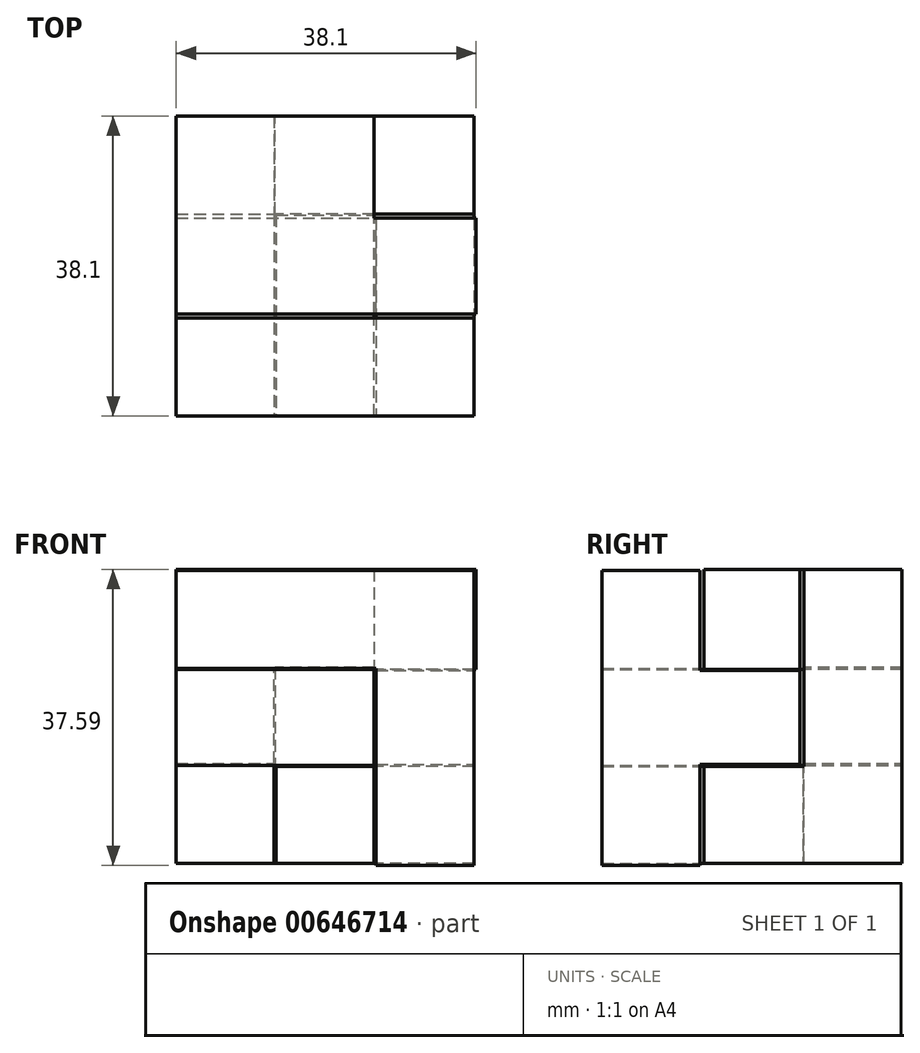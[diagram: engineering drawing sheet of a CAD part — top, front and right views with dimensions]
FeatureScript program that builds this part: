
annotation { "Feature Type Name" : "Feature", "Feature Type Description" : "" }
export const myFeature = defineFeature(function(context is Context, id is Id, definition is map)
    precondition{}
    {
        {
            var Q0;
            Q0=qCreatedBy(makeId("Top.planeOp"),FACE);
            var sketch = newSketch(context, id + "F0", { "sketchPlane" : qUnion([Q0])});
            skLineSegment(sketch, "E0.bottom", {"start": v(0, 0) * mm, "end": v(25.15, 0) * mm});
            skLineSegment(sketch, "E0.top", {"start": v(0, 25.15) * mm, "end": v(25.15, 25.15) * mm});
            skLineSegment(sketch, "E0.left", {"start": v(0, 0) * mm, "end": v(0, 25.15) * mm});
            skLineSegment(sketch, "E0.right", {"start": v(25.15, 0) * mm, "end": v(25.15, 25.15) * mm});
            skSolve(sketch);
        }
        {
            var Q0;
            Q0 = qSketchRegion(id + "F0", true);
            extrude(context, id + "F1", {"entities" : qUnion([Q0]), "depth" : 12.2 * mm, "offsetDistance" : 25.4 * mm});
        }
        {
            var Q0;
            Q0=qCreatedBy(makeId("Top.planeOp"),FACE);
            var sketch = newSketch(context, id + "F2", { "sketchPlane" : qUnion([Q0])});
            skLineSegment(sketch, "E1", {"start": v(0, 0) * mm, "end": v(0, 38.1) * mm});
            skLineSegment(sketch, "E2", {"start": v(0, 38.1) * mm, "end": v(25.15, 38.1) * mm});
            skLineSegment(sketch, "E3", {"start": v(25.15, 38.1) * mm, "end": v(25.15, 25.65) * mm});
            skLineSegment(sketch, "E4", {"start": v(25.15, 25.65) * mm, "end": v(12.45, 25.65) * mm});
            skLineSegment(sketch, "E5", {"start": v(12.45, 25.65) * mm, "end": v(12.45, 0) * mm});
            skLineSegment(sketch, "E6", {"start": v(12.45, 0) * mm, "end": v(0, 0) * mm});
            skSolve(sketch);
        }
        {
            var Q0;
            Q0 = qSketchRegion(id + "F2", true);
            extrude(context, id + "F3", {"entities" : qUnion([Q0]), "oppositeDirection" : true, "depth" : 12.45 * mm, "offsetDistance" : 25.4 * mm});
        }
        {
            var Q0;
            Q0=makeQuery(id+"F3.opExtrude","CAP_FACE",FACE,{"disambiguationData":[OSD([sQuery(id+"F2.wireOp",EDGE,"E1"),sQuery(id+"F2.wireOp",EDGE,"E2"),sQuery(id+"F2.wireOp",EDGE,"E3"),sQuery(id+"F2.wireOp",EDGE,"E4"),sQuery(id+"F2.wireOp",EDGE,"E5"),sQuery(id+"F2.wireOp",EDGE,"E6")])],"isStart":true});
            var sketch = newSketch(context, id + "F4", { "sketchPlane" : qUnion([Q0])});
            skLineSegment(sketch, "E7.bottom", {"start": v(25.15, 25.65) * mm, "end": v(12.57, 25.65) * mm});
            skLineSegment(sketch, "E7.top", {"start": v(25.15, 38.1) * mm, "end": v(12.57, 38.1) * mm});
            skLineSegment(sketch, "E7.left", {"start": v(25.15, 25.65) * mm, "end": v(25.15, 38.1) * mm});
            skLineSegment(sketch, "E7.right", {"start": v(12.57, 25.65) * mm, "end": v(12.57, 38.1) * mm});
            skSolve(sketch);
        }
        {
            var Q0;
            Q0 = qSketchRegion(id + "F4", true);
            extrude(context, id + "F5", {"entities" : qUnion([Q0]), "operationType" : NewBodyOperationType.ADD, "depth" : 12.45 * mm, "offsetDistance" : 25.4 * mm});
        }
        {
            var Q0;
            Q0=makeQuery(id+"F1.opExtrude","CAP_FACE",FACE,{"disambiguationData":[OSD([sQuery(id+"F0.wireOp",EDGE,"E0.bottom"),sQuery(id+"F0.wireOp",EDGE,"E0.top"),sQuery(id+"F0.wireOp",EDGE,"E0.left"),sQuery(id+"F0.wireOp",EDGE,"E0.right")])],"isStart":false});
            var sketch = newSketch(context, id + "F6", { "sketchPlane" : qUnion([Q0])});
            skLineSegment(sketch, "E8", {"start": v(0, 38.1) * mm, "end": v(25.15, 38.1) * mm});
            skLineSegment(sketch, "E9", {"start": v(25.15, 38.1) * mm, "end": v(25.15, 25.15) * mm});
            skLineSegment(sketch, "E10", {"start": v(25.15, 25.15) * mm, "end": v(38.1, 25.15) * mm});
            skLineSegment(sketch, "E11", {"start": v(38.1, 25.15) * mm, "end": v(38.1, 12.95) * mm});
            skLineSegment(sketch, "E12", {"start": v(38.1, 12.95) * mm, "end": v(12.95, 12.95) * mm});
            skLineSegment(sketch, "E13", {"start": v(12.95, 12.95) * mm, "end": v(12.95, 25.15) * mm, "construction": true});
            skLineSegment(sketch, "E14", {"start": v(12.95, 25.15) * mm, "end": v(0, 25.15) * mm, "construction": true});
            skLineSegment(sketch, "E15", {"start": v(0, 25.15) * mm, "end": v(0, 38.1) * mm});
            skLineSegment(sketch, "E16", {"start": v(12.95, 12.95) * mm, "end": v(0, 12.95) * mm});
            skLineSegment(sketch, "E17", {"start": v(0, 12.95) * mm, "end": v(0, 25.15) * mm});
            skSolve(sketch);
        }
        {
            var Q0;
            Q0 = qSketchRegion(id + "F6", true);
            extrude(context, id + "F7", {"entities" : qUnion([Q0]), "depth" : 12.7 * mm, "offsetDistance" : 25.4 * mm});
        }
        {
            var Q0;
            Q0=makeQuery(id+"F7.opExtrude","CAP_FACE",FACE,{"disambiguationData":[OSD([sQuery(id+"F6.wireOp",EDGE,"E8"),sQuery(id+"F6.wireOp",EDGE,"E9"),sQuery(id+"F6.wireOp",EDGE,"E10"),sQuery(id+"F6.wireOp",EDGE,"E11"),sQuery(id+"F6.wireOp",EDGE,"E12"),sQuery(id+"F6.wireOp",EDGE,"E13"),sQuery(id+"F6.wireOp",EDGE,"E14"),sQuery(id+"F6.wireOp",EDGE,"E15")])],"isStart":true});
            var sketch = newSketch(context, id + "F8", { "sketchPlane" : qUnion([Q0])});
            skLineSegment(sketch, "E18.bottom", {"start": v(0, -38.1) * mm, "end": v(12.45, -38.1) * mm});
            skLineSegment(sketch, "E18.top", {"start": v(0, -25.65) * mm, "end": v(12.45, -25.65) * mm});
            skLineSegment(sketch, "E18.left", {"start": v(0, -38.1) * mm, "end": v(0, -25.65) * mm});
            skLineSegment(sketch, "E18.right", {"start": v(12.45, -38.1) * mm, "end": v(12.45, -25.65) * mm});
            skSolve(sketch);
        }
        {
            var Q0;
            Q0 = qSketchRegion(id + "F8", true);
            extrude(context, id + "F9", {"entities" : qUnion([Q0]), "operationType" : NewBodyOperationType.ADD, "depth" : 11.94 * mm, "offsetDistance" : 25.4 * mm});
        }
        {
            var Q0;
            Q0=makeQuery(id+"F5.boolean.opBoolean","MERGE",FACE,{"derivedFrom":[makeQuery(id+"F3.opExtrude","SWEPT_FACE",FACE,{"disambiguationData":[OSD([sQuery(id+"F2.wireOp",EDGE,"E3")])]}),makeQuery(id+"F5.opExtrude","SWEPT_FACE",FACE,{"disambiguationData":[OSD([sQuery(id+"F4.wireOp",EDGE,"E7.left")])]})]});
            var sketch = newSketch(context, id + "F10", { "sketchPlane" : qUnion([Q0])});
            skLineSegment(sketch, "E19", {"start": v(38.1, -12.45) * mm, "end": v(38.1, 24.9) * mm});
            skLineSegment(sketch, "E20", {"start": v(38.1, 24.9) * mm, "end": v(25.65, 24.9) * mm});
            skLineSegment(sketch, "E21", {"start": v(25.65, 24.9) * mm, "end": v(25.65, -0.13) * mm});
            skLineSegment(sketch, "E22", {"start": v(25.65, -0.13) * mm, "end": v(12.95, -0.13) * mm});
            skLineSegment(sketch, "E23", {"start": v(12.95, -0.13) * mm, "end": v(12.95, -12.45) * mm});
            skLineSegment(sketch, "E24", {"start": v(12.95, -12.45) * mm, "end": v(38.1, -12.45) * mm});
            skSolve(sketch);
        }
        {
            var Q0;
            Q0 = qSketchRegion(id + "F10", true);
            extrude(context, id + "F11", {"entities" : qUnion([Q0]), "depth" : 12.7 * mm, "offsetDistance" : 25.4 * mm});
        }
        {
            var Q0;
            Q0=makeQuery(id+"F11.opExtrude","CAP_FACE",FACE,{"disambiguationData":[OSD([sQuery(id+"F10.wireOp",EDGE,"E19"),sQuery(id+"F10.wireOp",EDGE,"E20"),sQuery(id+"F10.wireOp",EDGE,"E21"),sQuery(id+"F10.wireOp",EDGE,"E22"),sQuery(id+"F10.wireOp",EDGE,"E23"),sQuery(id+"F10.wireOp",EDGE,"E24")])],"isStart":false});
            var sketch = newSketch(context, id + "F12", { "sketchPlane" : qUnion([Q0])});
            skLineSegment(sketch, "E25.bottom", {"start": v(12.95, -0.13) * mm, "end": v(25.53, -0.13) * mm});
            skLineSegment(sketch, "E25.top", {"start": v(12.95, -12.45) * mm, "end": v(25.53, -12.45) * mm});
            skLineSegment(sketch, "E25.left", {"start": v(12.95, -0.13) * mm, "end": v(12.95, -12.45) * mm});
            skLineSegment(sketch, "E25.right", {"start": v(25.53, -0.13) * mm, "end": v(25.53, -12.45) * mm});
            skSolve(sketch);
        }
        {
            var Q0;
            Q0 = qSketchRegion(id + "F12", true);
            extrude(context, id + "F13", {"entities" : qUnion([Q0]), "operationType" : NewBodyOperationType.ADD, "oppositeDirection" : true, "depth" : 25.15 * mm, "offsetDistance" : 25.4 * mm});
        }
        {
            var Q0;
            Q0=makeQuery(id+"F13.boolean.opBoolean","MERGE",FACE,{"derivedFrom":[makeQuery(id+"F11.opExtrude","SWEPT_FACE",FACE,{"disambiguationData":[OSD([sQuery(id+"F10.wireOp",EDGE,"E23")])]}),makeQuery(id+"F13.opExtrude","SWEPT_FACE",FACE,{"disambiguationData":[OSD([sQuery(id+"F12.wireOp",EDGE,"E25.left")])]})]});
            var sketch = newSketch(context, id + "F14", { "sketchPlane" : qUnion([Q0])});
            skLineSegment(sketch, "E26.bottom", {"start": v(12.7, -0.13) * mm, "end": v(25.15, -0.13) * mm});
            skLineSegment(sketch, "E26.top", {"start": v(12.7, -12.45) * mm, "end": v(25.15, -12.45) * mm});
            skLineSegment(sketch, "E26.left", {"start": v(12.7, -0.13) * mm, "end": v(12.7, -12.45) * mm});
            skLineSegment(sketch, "E26.right", {"start": v(25.15, -0.13) * mm, "end": v(25.15, -12.45) * mm});
            skSolve(sketch);
        }
        {
            var Q0;
            Q0 = qSketchRegion(id + "F14", true);
            extrude(context, id + "F15", {"entities" : qUnion([Q0]), "operationType" : NewBodyOperationType.ADD, "depth" : 12.95 * mm, "offsetDistance" : 25.4 * mm});
        }
        {
            var Q0;
            Q0=makeQuery(id+"F11.opExtrude","CAP_FACE",FACE,{"disambiguationData":[OSD([sQuery(id+"F10.wireOp",EDGE,"E19"),sQuery(id+"F10.wireOp",EDGE,"E20"),sQuery(id+"F10.wireOp",EDGE,"E21"),sQuery(id+"F10.wireOp",EDGE,"E22"),sQuery(id+"F10.wireOp",EDGE,"E23"),sQuery(id+"F10.wireOp",EDGE,"E24")])],"isStart":false});
            var sketch = newSketch(context, id + "F16", { "sketchPlane" : qUnion([Q0])});
            skLineSegment(sketch, "E27", {"start": v(0, -12.7) * mm, "end": v(0, 24.76) * mm});
            skLineSegment(sketch, "E28", {"start": v(0, 24.76) * mm, "end": v(12.45, 24.77) * mm});
            skLineSegment(sketch, "E29", {"start": v(12.45, 24.76) * mm, "end": v(12.45, 12.06) * mm});
            skLineSegment(sketch, "E30", {"start": v(12.45, 12.06) * mm, "end": v(25.15, 12.07) * mm});
            skLineSegment(sketch, "E31", {"start": v(25.15, 12.07) * mm, "end": v(25.15, 0.13) * mm});
            skLineSegment(sketch, "E32", {"start": v(25.15, 0.13) * mm, "end": v(12.45, 0.13) * mm});
            skLineSegment(sketch, "E33", {"start": v(12.45, 0.13) * mm, "end": v(12.45, -12.7) * mm});
            skLineSegment(sketch, "E34", {"start": v(12.45, -12.7) * mm, "end": v(0, -12.7) * mm});
            skSolve(sketch);
        }
        {
            var Q0;
            Q0 = qSketchRegion(id + "F16", true);
            extrude(context, id + "F17", {"entities" : qUnion([Q0]), "oppositeDirection" : true, "depth" : 12.45 * mm, "offsetDistance" : 25.4 * mm});
        }
        {
            var Q0;
            Q0=makeQuery(id+"F17.opExtrude","CAP_FACE",FACE,{"disambiguationData":[OSD([sQuery(id+"F16.wireOp",EDGE,"E27"),sQuery(id+"F16.wireOp",EDGE,"E28"),sQuery(id+"F16.wireOp",EDGE,"E29"),sQuery(id+"F16.wireOp",EDGE,"E30"),sQuery(id+"F16.wireOp",EDGE,"E31"),sQuery(id+"F16.wireOp",EDGE,"E32"),sQuery(id+"F16.wireOp",EDGE,"E33"),sQuery(id+"F16.wireOp",EDGE,"E34")])],"isStart":false});
            var sketch = newSketch(context, id + "F18", { "sketchPlane" : qUnion([Q0])});
            skLineSegment(sketch, "E35.bottom", {"start": v(0, 24.76) * mm, "end": v(-12.45, 24.76) * mm});
            skLineSegment(sketch, "E35.top", {"start": v(0, 12.32) * mm, "end": v(-12.45, 12.32) * mm});
            skLineSegment(sketch, "E35.left", {"start": v(0, 24.76) * mm, "end": v(0, 12.32) * mm});
            skLineSegment(sketch, "E35.right", {"start": v(-12.45, 24.76) * mm, "end": v(-12.45, 12.32) * mm});
            skSolve(sketch);
        }
        {
            var Q0;
            Q0 = qSketchRegion(id + "F18", true);
            extrude(context, id + "F19", {"entities" : qUnion([Q0]), "operationType" : NewBodyOperationType.ADD, "depth" : 25.4 * mm, "offsetDistance" : 25.4 * mm});
        }
    });
